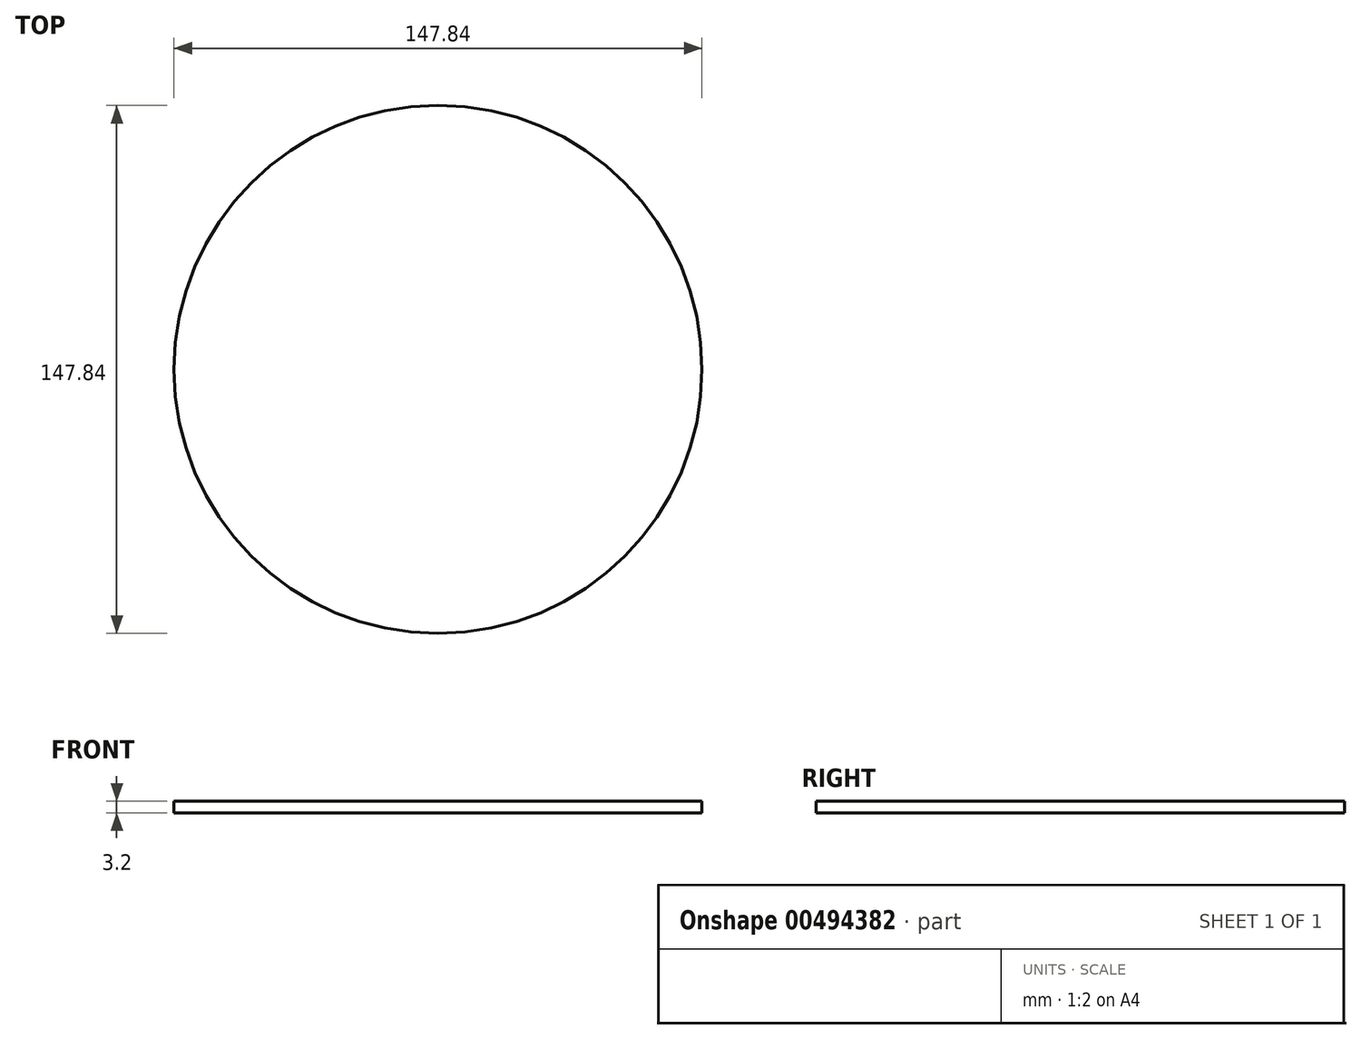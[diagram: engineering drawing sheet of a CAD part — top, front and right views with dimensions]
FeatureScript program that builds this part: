
annotation { "Feature Type Name" : "Feature", "Feature Type Description" : "" }
export const myFeature = defineFeature(function(context is Context, id is Id, definition is map)
    precondition{}
    {
        {
            var Q0;
            Q0=qCreatedBy(makeId("Top.planeOp"),FACE);
            var sketch = newSketch(context, id + "F0", { "sketchPlane" : qUnion([Q0])});
            skCircle(sketch, "E0", {"center": v(0, 0) * mm, "radius": 73.92 * mm});
            skSolve(sketch);
        }
        {
            var Q0;
            Q0=qSketchRegion(id+"F0",true);
            extrude(context, id + "F1", {"entities" : qUnion([Q0]), "depth" : 3.2 * mm});
        }
    });
